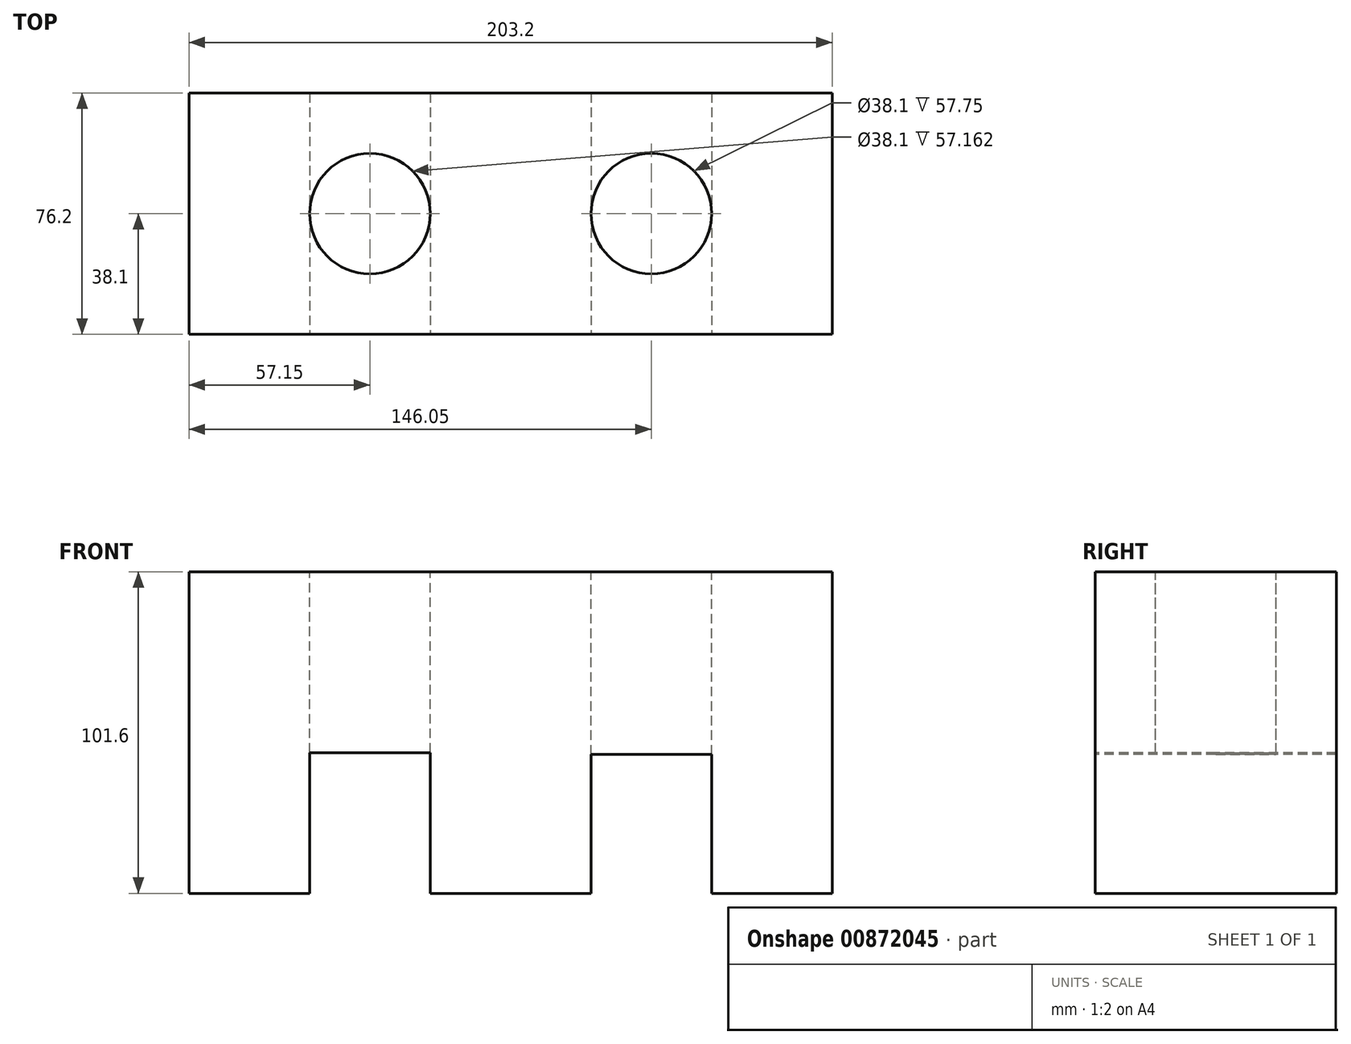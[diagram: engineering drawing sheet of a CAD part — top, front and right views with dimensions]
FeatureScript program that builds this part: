
annotation { "Feature Type Name" : "Feature", "Feature Type Description" : "" }
export const myFeature = defineFeature(function(context is Context, id is Id, definition is map)
    precondition{}
    {
        {
            var Q0;
            Q0=qCreatedBy(makeId("Front.planeOp"),FACE);
            var sketch = newSketch(context, id + "F0", { "sketchPlane" : qUnion([Q0])});
            skLineSegment(sketch, "E0", {"start": v(0, 0) * mm, "end": v(38.1, 0) * mm});
            skLineSegment(sketch, "E1", {"start": v(38.1, 0) * mm, "end": v(38.1, 44.44) * mm});
            skLineSegment(sketch, "E2", {"start": v(38.1, 44.44) * mm, "end": v(76.2, 44.44) * mm});
            skLineSegment(sketch, "E3", {"start": v(76.2, 44.44) * mm, "end": v(76.2, 0) * mm});
            skLineSegment(sketch, "E4", {"start": v(76.2, 0) * mm, "end": v(127, 0) * mm});
            skLineSegment(sketch, "E5", {"start": v(127, 0) * mm, "end": v(127, 43.85) * mm});
            skLineSegment(sketch, "E6", {"start": v(127, 43.85) * mm, "end": v(165.1, 43.85) * mm});
            skLineSegment(sketch, "E7", {"start": v(165.1, 43.85) * mm, "end": v(165.1, 0) * mm});
            skLineSegment(sketch, "E8", {"start": v(165.1, 0) * mm, "end": v(203.2, 0) * mm});
            skLineSegment(sketch, "E9", {"start": v(203.2, 0) * mm, "end": v(203.2, 101.6) * mm});
            skLineSegment(sketch, "E10", {"start": v(203.2, 101.6) * mm, "end": v(0, 101.6) * mm});
            skLineSegment(sketch, "E11", {"start": v(0, 101.6) * mm, "end": v(0, 0) * mm});
            skSolve(sketch);
        }
        {
            var Q0;
            Q0=makeQuery(id+"F0.imprint","IMPRINT",FACE,{"disambiguationData":[TD([[makeQuery(id+"F0.imprint","IMPRINT",EDGE,{"derivedFrom":sQuery(id+"F0.wireOp",EDGE,"E0")}),1.0]])]});
            extrude(context, id + "F1", {"entities" : qUnion([Q0]), "oppositeDirection" : true, "depth" : 76.2 * mm, "offsetDistance" : 25.4 * mm});
        }
        {
            var Q0;
            Q0=makeQuery(id+"F1.opExtrude","SWEPT_FACE",FACE,{"disambiguationData":[OSD([sQuery(id+"F0.wireOp",EDGE,"E10")])]});
            var sketch = newSketch(context, id + "F2", { "sketchPlane" : qUnion([Q0])});
            skLineSegment(sketch, "E12", {"start": v(0, 38.1) * mm, "end": v(57.15, 38.1) * mm});
            skLineSegment(sketch, "E13", {"start": v(146.05, 38.1) * mm, "end": v(203.2, 38.1) * mm});
            skLineSegment(sketch, "E14", {"start": v(203.2, 38.1) * mm, "end": v(146.05, 38.1) * mm});
            skSolve(sketch);
        }
        {
            var Q0;
            Q0=sQuery(id+"F2.wireOp",VERTEX,"E12.end");
            var Q1;
            Q1=sQuery(id+"F2.wireOp",VERTEX,"E13.start");
            var Q2;
            Q2=makeQuery(id+"F1.opExtrude","SWEPT_BODY",BODY,{"disambiguationData":[OSD([sQuery(id+"F0.wireOp",EDGE,"E0"),sQuery(id+"F0.wireOp",EDGE,"E1"),sQuery(id+"F0.wireOp",EDGE,"E2"),sQuery(id+"F0.wireOp",EDGE,"E3"),sQuery(id+"F0.wireOp",EDGE,"E4"),sQuery(id+"F0.wireOp",EDGE,"E5"),sQuery(id+"F0.wireOp",EDGE,"E6"),sQuery(id+"F0.wireOp",EDGE,"E7"),sQuery(id+"F0.wireOp",EDGE,"E8"),sQuery(id+"F0.wireOp",EDGE,"E9"),sQuery(id+"F0.wireOp",EDGE,"E10"),sQuery(id+"F0.wireOp",EDGE,"E11")])]});
            hole(context, id + "F3", {"style" : HoleStyle.SIMPLE, "endStyle" : HoleEndStyle.THROUGH, "holeDiameter" : 38.1 * mm, "majorDiameter" : 6.35 * mm, "isTappedThrough" : true, "tappedDepth" : 12.7 * mm, "tapClearance" : 3, "locations" : qUnion([Q0, Q1]), "scope" : qUnion([Q2])});
        }
    });
